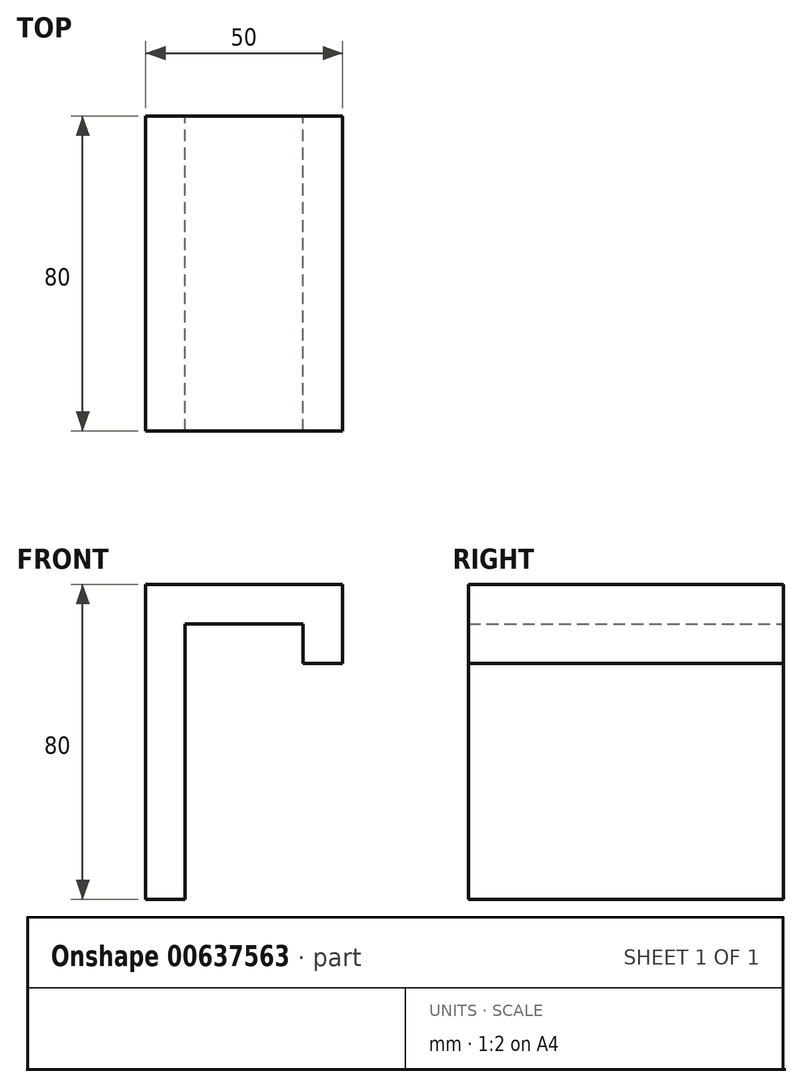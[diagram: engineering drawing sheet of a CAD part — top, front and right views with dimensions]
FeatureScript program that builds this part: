
annotation { "Feature Type Name" : "Feature", "Feature Type Description" : "" }
export const myFeature = defineFeature(function(context is Context, id is Id, definition is map)
    precondition{}
    {
        {
            var Q0;
            Q0=qCreatedBy(makeId("Front.planeOp"),FACE);
            var sketch = newSketch(context, id + "F0", { "sketchPlane" : qUnion([Q0])});
            skLineSegment(sketch, "E0", {"start": v(-58.86, 40.86) * mm, "end": v(-58.86, -39.14) * mm});
            skLineSegment(sketch, "E1", {"start": v(-58.86, 40.86) * mm, "end": v(-8.86, 40.86) * mm});
            skLineSegment(sketch, "E2", {"start": v(-8.86, 40.86) * mm, "end": v(-8.86, 20.86) * mm});
            skLineSegment(sketch, "E3", {"start": v(-8.86, 20.86) * mm, "end": v(-18.86, 20.86) * mm});
            skLineSegment(sketch, "E4", {"start": v(-18.86, 20.86) * mm, "end": v(-18.86, 30.86) * mm});
            skLineSegment(sketch, "E5", {"start": v(-18.86, 30.86) * mm, "end": v(-48.86, 30.86) * mm});
            skLineSegment(sketch, "E6", {"start": v(-48.86, 30.86) * mm, "end": v(-48.86, -39.14) * mm});
            skLineSegment(sketch, "E7", {"start": v(-58.86, -39.14) * mm, "end": v(-48.86, -39.14) * mm});
            skSolve(sketch);
        }
        {
            var Q0;
            Q0 = qSketchRegion(id + "F0", true);
            extrude(context, id + "F1", {"entities" : qUnion([Q0]), "depth" : 80 * mm, "offsetDistance" : 25 * mm});
        }
    });
